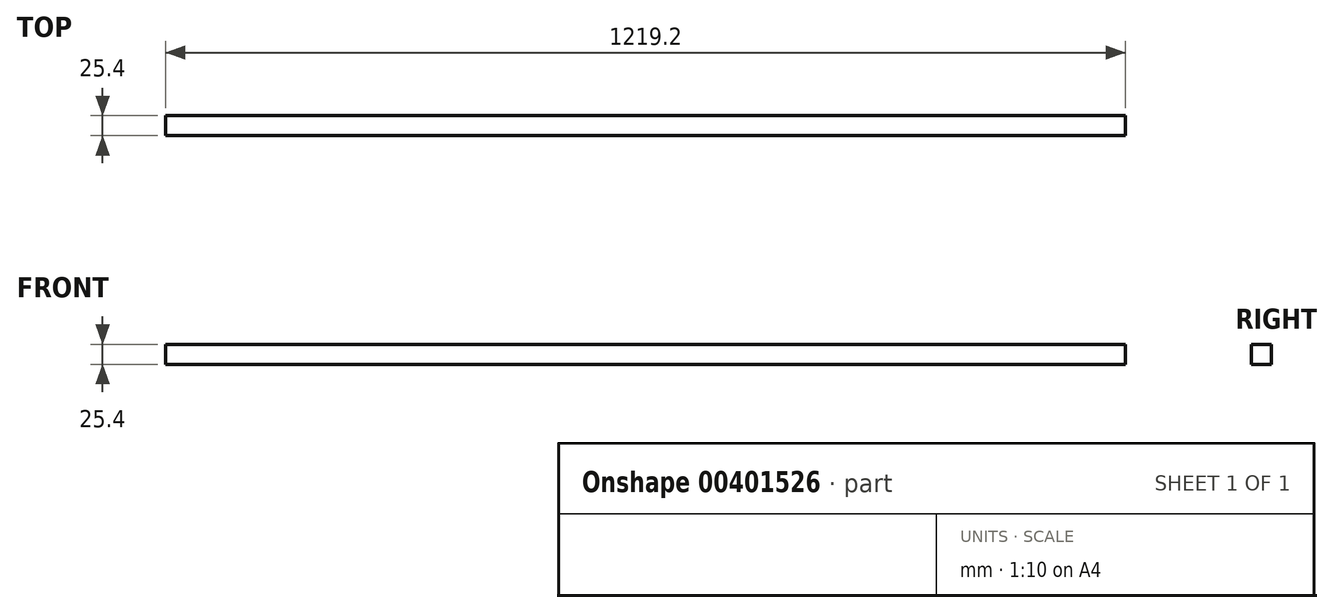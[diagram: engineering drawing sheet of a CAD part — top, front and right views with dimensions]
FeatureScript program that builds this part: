
annotation { "Feature Type Name" : "Feature", "Feature Type Description" : "" }
export const myFeature = defineFeature(function(context is Context, id is Id, definition is map)
    precondition{}
    {
        {
            var Q0;
            Q0=qCreatedBy(makeId("Front.planeOp"),FACE);
            var sketch = newSketch(context, id + "F0", { "sketchPlane" : qUnion([Q0])});
            skLineSegment(sketch, "E0.bottom", {"start": v(-600.4, 12.7) * mm, "end": v(618.8, 12.7) * mm});
            skLineSegment(sketch, "E0.top", {"start": v(-600.4, -12.7) * mm, "end": v(618.8, -12.7) * mm});
            skLineSegment(sketch, "E0.left", {"start": v(-600.4, 12.7) * mm, "end": v(-600.4, -12.7) * mm});
            skLineSegment(sketch, "E0.right", {"start": v(618.8, 12.7) * mm, "end": v(618.8, -12.7) * mm});
            skPoint(sketch, "E0.middle", {"position": v(9.2, 0) * mm});
            skSolve(sketch);
        }
        {
            var Q0;
            Q0=makeQuery(id+"F0.imprint","IMPRINT",FACE,{"disambiguationData":[TD([[makeQuery(id+"F0.imprint","IMPRINT",EDGE,{"derivedFrom":sQuery(id+"F0.wireOp",EDGE,"E0.bottom")}),-1.0]])]});
            extrude(context, id + "F1", {"entities" : qUnion([Q0]), "depth" : 25.4 * mm});
        }
    });
